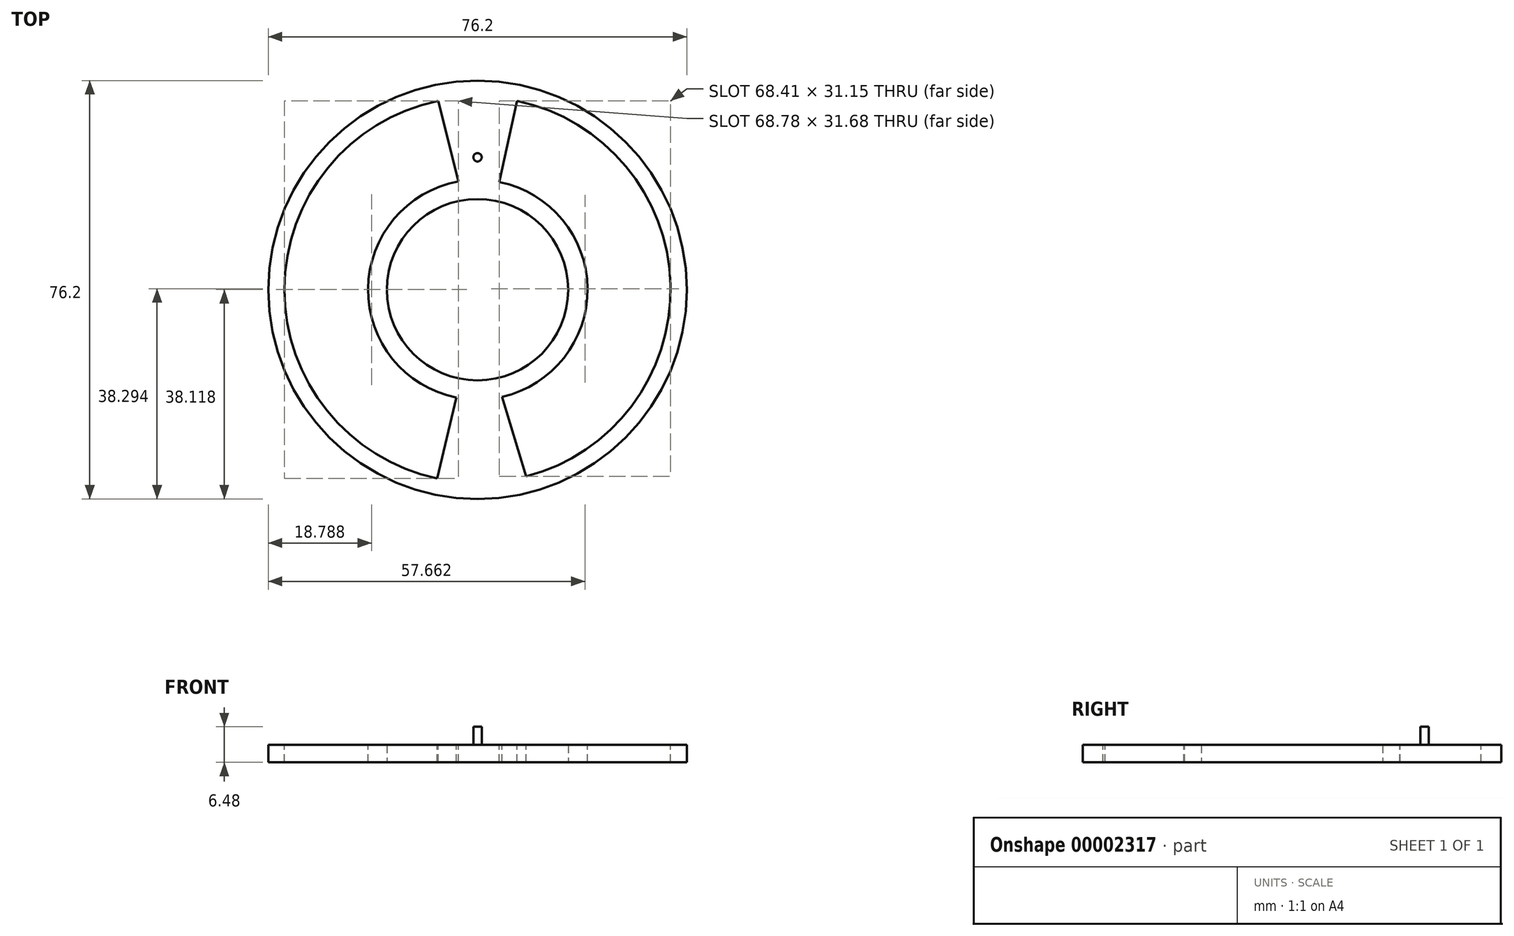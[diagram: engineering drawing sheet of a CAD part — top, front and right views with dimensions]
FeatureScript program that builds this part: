
annotation { "Feature Type Name" : "Feature", "Feature Type Description" : "" }
export const myFeature = defineFeature(function(context is Context, id is Id, definition is map)
    precondition{}
    {
        {
            var Q0;
            Q0=qCreatedBy(makeId("Top.planeOp"),FACE);
            var sketch = newSketch(context, id + "F0", { "sketchPlane" : qUnion([Q0])});
            skCircle(sketch, "E0", {"center": v(0, 0) * mm, "radius": 38.1 * mm});
            skSolve(sketch);
        }
        {
            var Q0;
            Q0=makeQuery(id+"F0.imprint","IMPRINT",FACE,{"disambiguationData":[TD([[makeQuery(id+"F0.imprint","IMPRINT",EDGE,{"derivedFrom":sQuery(id+"F0.wireOp",EDGE,"E0")}),1.0]])]});
            extrude(context, id + "F1", {"entities" : qUnion([Q0]), "depth" : 3.17 * mm});
        }
        {
            var Q0;
            Q0=makeQuery(id+"F1.opExtrude","CAP_FACE",FACE,{"disambiguationData":[OSD([sQuery(id+"F0.wireOp",EDGE,"E0")])],"isStart":false});
            var sketch = newSketch(context, id + "F2", { "sketchPlane" : qUnion([Q0])});
            skCircle(sketch, "E1", {"center": v(0, 6.35) * mm, "radius": 1 * mm});
            skCircle(sketch, "E2", {"center": v(0, 24.13) * mm, "radius": 0.76 * mm});
            skSolve(sketch);
        }
        {
            var Q0;
            {Q0=qUnion([makeQuery(id+"F2.imprint","IMPRINT",FACE,{"disambiguationData":[TD([[makeQuery(id+"F2.imprint","IMPRINT",EDGE,{"derivedFrom":sQuery(id+"F2.wireOp",EDGE,"E1")}),1.0]])]}),makeQuery(id+"F2.imprint","IMPRINT",FACE,{"disambiguationData":[TD([[makeQuery(id+"F2.imprint","IMPRINT",EDGE,{"derivedFrom":sQuery(id+"F2.wireOp",EDGE,"E2")}),1.0]])]})]);}
            extrude(context, id + "F3", {"entities" : qUnion([Q0]), "operationType" : NewBodyOperationType.ADD, "depth" : 3.3 * mm});
        }
        {
            var Q0;
            Q0=qCreatedBy(makeId("Top.planeOp"),FACE);
            var sketch = newSketch(context, id + "F4", { "sketchPlane" : qUnion([Q0])});
            skCircle(sketch, "E3", {"center": v(0, 0) * mm, "radius": 16.51 * mm});
            skSolve(sketch);
        }
        {
            var Q0;
            Q0=makeQuery(id+"F4.imprint","IMPRINT",FACE,{"disambiguationData":[TD([[makeQuery(id+"F4.imprint","IMPRINT",EDGE,{"derivedFrom":sQuery(id+"F4.wireOp",EDGE,"E3")}),1.0]])]});
            var Q1;
            Q1=makeQuery(id+"F3.opExtrude","CAP_FACE",FACE,{"disambiguationData":[OSD([sQuery(id+"F2.wireOp",EDGE,"E1")])],"isStart":false});
            extrude(context, id + "F5", {"entities" : qUnion([Q0]), "endBound" : BoundingType.UP_TO_SURFACE, "endBoundEntityFace" : qUnion([Q1]), "depth" : 25.4 * mm});
        }
        {
            var Q0;
            Q0=makeQuery(id+"F5.opExtrude","SWEPT_BODY",BODY,{"disambiguationData":[OSD([sQuery(id+"F4.wireOp",EDGE,"E3")])]});
            var Q1;
            Q1=makeQuery(id+"F1.opExtrude","SWEPT_BODY",BODY,{"disambiguationData":[OSD([sQuery(id+"F0.wireOp",EDGE,"E0")])]});
            booleanBodies(context, id + "F6", {"operationType" : BooleanOperationType.SUBTRACTION, "tools" : qUnion([Q0]), "targets" : qUnion([Q1])});
        }
        {
            var Q0;
            Q0=makeQuery(id+"F1.opExtrude","CAP_FACE",FACE,{"disambiguationData":[OSD([sQuery(id+"F0.wireOp",EDGE,"E0")])],"isStart":false});
            var sketch = newSketch(context, id + "F7", { "sketchPlane" : qUnion([Q0])});
            skLineSegment(sketch, "E4", {"start": v(-7.17, 34.4) * mm, "end": v(-3.47, 19.72) * mm});
            skLineSegment(sketch, "E5", {"start": v(3.99, 19.62) * mm, "end": v(7.2, 34.4) * mm});
            skLineSegment(sketch, "E6", {"start": v(-3.84, -19.65) * mm, "end": v(-7.34, -34.37) * mm});
            skLineSegment(sketch, "E7", {"start": v(4.47, -19.52) * mm, "end": v(8.86, -34.01) * mm});
            skArc(sketch, "E8", {"start": v(4.47, -19.52) * mm, "mid": v(20.03, 0.25) * mm, "end": v(3.99, 19.62) * mm});
            skArc(sketch, "E9", {"start": v(-3.47, 19.72) * mm, "mid": v(-19.92, 0.19) * mm, "end": v(-3.84, -19.65) * mm});
            skArc(sketch, "E10", {"start": v(-7.17, 34.4) * mm, "mid": v(-35.15, 0.09) * mm, "end": v(-7.34, -34.37) * mm});
            skArc(sketch, "E11", {"start": v(8.86, -34.01) * mm, "mid": v(35.14, 0.85) * mm, "end": v(7.2, 34.4) * mm});
            skSolve(sketch);
        }
        {
            var Q0;
            {Q0=qUnion([makeQuery(id+"F7.imprint","IMPRINT",FACE,{"disambiguationData":[TD([[makeQuery(id+"F7.imprint","IMPRINT",EDGE,{"derivedFrom":sQuery(id+"F7.wireOp",EDGE,"E4")}),-1.0]])]}),makeQuery(id+"F7.imprint","IMPRINT",FACE,{"disambiguationData":[TD([[makeQuery(id+"F7.imprint","IMPRINT",EDGE,{"derivedFrom":sQuery(id+"F7.wireOp",EDGE,"E5")}),-1.0]])]})]);}
            extrude(context, id + "F8", {"entities" : qUnion([Q0]), "operationType" : NewBodyOperationType.REMOVE, "oppositeDirection" : true, "depth" : 25.4 * mm});
        }
    });
